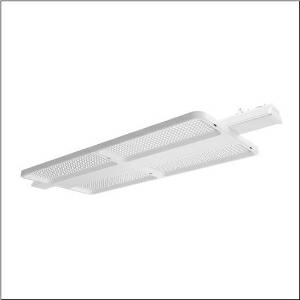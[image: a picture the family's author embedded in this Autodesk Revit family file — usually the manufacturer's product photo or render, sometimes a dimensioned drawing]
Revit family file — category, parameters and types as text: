
# Revit family: highbay_11_fur_licross_tragschiene_maxi_51hn12db5vla
name_source: partatom
category: Lighting Fixtures
units: mm (PartAtom-declared; Revit-internal decimal feet)

## family parameters
Cut with Voids When Loaded = No
Host = Face
Light Source = No
Part Type = Normal
Room Calculation Point = No
Round Connector Dimension = Use Diameter
Shared = No

## types (1)
- --- (1 x LED, 55810 lm, 294.9 W, 5000K)
    Apparent Load = 295 VA
    CIE Flux Codes = 87 98 100 100 100
    Color Rendering = 80
    Color Temperature = 5000K
    Default Elevation = 1800 mm
    Description = high bay luminaire Highbay 11 for Licross trunking rail maxi; direct symmetric wide distribution, light control with lens of PMMA; UGR ≤ 22 (X = 4H | Y = 8H | S = 0.25H | reflection values 70/50/20); luminous flux: 55.810lm; light colour: 850, colour temperature: 5000K, MacAdam ≤ 2 SDCM (initial), colour rendering: CRI > 80; luminous efficacy: 189,3lm/W; rated service life: 100.000h (L95) at AT= 25°C; control: DALI 2; luminaire connection: plug, 5-pole, with phase selectionmains connection: 230..240V, AC 50/60Hz; connected load: 294,9W; protection rating (complete): IP64; insulation class (complete): insulation class I (protective earthing); protection symbol: D; impact resistance: IK06; certification: CE, ENEC, VDE, UKCA; internal wiring halogen-free; luminaire LABS conformity tested according to VDMA 24364:2018-05; Suitable for use in the food industry according to the specifications of IFS-Food, HACCP and/or BRC; housing frame of high-performance plastic PA6, matt traffic white (RAL 9016); cover of PMMA; fixing on rail side of steel, galvanised, white; blank cover of PC/ABS, traffic white (RAL 9016); dimension (LxWxH): 1.250 x 442 x 71mm; permissible operating ambient temperature: -40..+50°C (reducing of maximum allowable ambient temperature of 5°C with ceiling mounting); packaging unit: 1 piece
    Height = 72 mm  [stored 0.23622 ft]
    Lamp = 1 x LED
    Lamp Light Flux = 55810 lm
    Lamp Power = 294.9 W
    Lamp count = 1
    Length = 946 mm
    Luminous efficacy = 189 lm/W
    Manufacturer = Siteco
    ModVariant = No
    Model = 51HN12DB5VLA
    Mounting Place = Ceiling
    Mounting Type = Pendant
    Number of Poles = 1
    OnlyDefault = Yes
    Power Factor = 1
    Product Name = Highbay 11 für Licross Tragschiene maxi
    Product group = high bay luminaire
    ProductGroupID = 902
    Protection Class = Protection class I
    Protection Degree = IP 64
    RLX_Detail_Level = 1
    RLX_Emergency_Light_Flux = 0 lm
    RLX_Emergency_Type = 0
    RLX_Emergency_Type_DB = No
    RlxData = <blob elided: 24277 chars, md5=a6f20247>
    Socket = socket
    Standby Power = 0 W
    System Light Flux = 55810 lm
    System Power = 295 W
    Type Comments = factory setting: luminous flux: 100 % | dim-lin: 254 | 664 mA
    Type Image = l_1361711.jpg
    URL = http://relux.com
    VarID = @adj_006963
    Voltage = 0 V
    Weight = 0.00 kg
    Width = 442 mm

note: [stored X ft] marks values corroborated as IEEE doubles in the binary element streams (Revit-internal decimal feet)

## geometry (parser evidence)
native form markers: Blend x4, Sweep x10
no freeform markers — native parametric forms only
